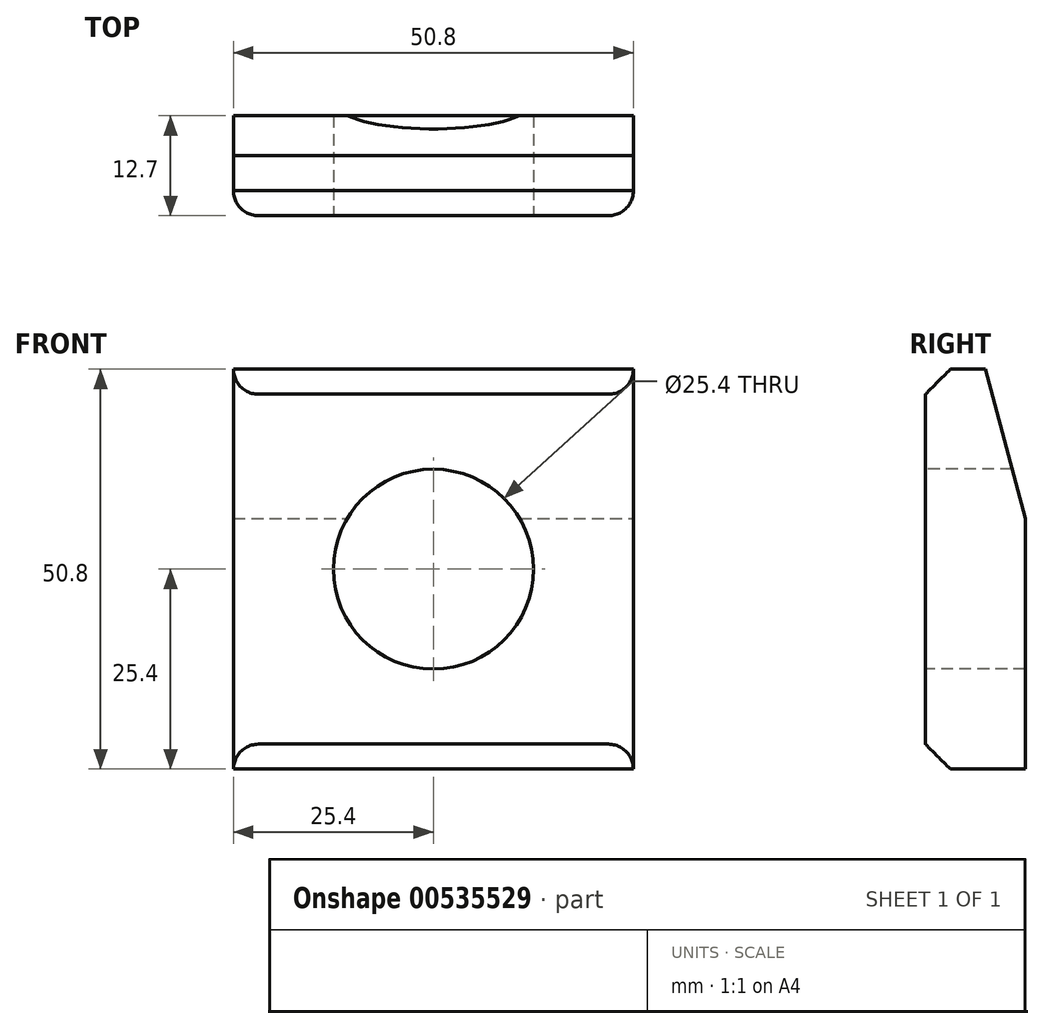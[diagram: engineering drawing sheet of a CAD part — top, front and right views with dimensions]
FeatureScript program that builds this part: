
annotation { "Feature Type Name" : "Feature", "Feature Type Description" : "" }
export const myFeature = defineFeature(function(context is Context, id is Id, definition is map)
    precondition{}
    {
        {
            var Q0;
            Q0=qCreatedBy(makeId("Front.planeOp"),FACE);
            var sketch = newSketch(context, id + "F0", { "sketchPlane" : qUnion([Q0])});
            skLineSegment(sketch, "E0.bottom", {"start": v(0, 0) * mm, "end": v(50.8, 0) * mm});
            skLineSegment(sketch, "E0.top", {"start": v(0, -50.8) * mm, "end": v(50.8, -50.8) * mm});
            skLineSegment(sketch, "E0.left", {"start": v(0, 0) * mm, "end": v(0, -50.8) * mm});
            skLineSegment(sketch, "E0.right", {"start": v(50.8, 0) * mm, "end": v(50.8, -50.8) * mm});
            skSolve(sketch);
        }
        {
            var Q0;
            Q0 = qSketchRegion(id + "F0", true);
            extrude(context, id + "F1", {"entities" : qUnion([Q0]), "depth" : 12.7 * mm, "offsetDistance" : 25.4 * mm});
        }
        {
            var Q0;
            Q0=makeQuery(id+"F1.opExtrude","CAP_FACE",FACE,{"disambiguationData":[OSD([sQuery(id+"F0.wireOp",EDGE,"E0.bottom"),sQuery(id+"F0.wireOp",EDGE,"E0.top"),sQuery(id+"F0.wireOp",EDGE,"E0.left"),sQuery(id+"F0.wireOp",EDGE,"E0.right")])],"isStart":false});
            var sketch = newSketch(context, id + "F2", { "sketchPlane" : qUnion([Q0])});
            skCircle(sketch, "E1", {"center": v(25.4, -25.4) * mm, "radius": 12.7 * mm});
            skSolve(sketch);
        }
        {
            var Q0;
            Q0 = qSketchRegion(id + "F2", true);
            extrude(context, id + "F3", {"entities" : qUnion([Q0]), "operationType" : NewBodyOperationType.REMOVE, "oppositeDirection" : true, "depth" : 25.4 * mm, "offsetDistance" : 25.4 * mm});
        }
        {
            var Q0;
            Q0=makeQuery(id+"F1.opExtrude","CAP_EDGE",EDGE,{"disambiguationData":[OSD([sQuery(id+"F0.wireOp",EDGE,"E0.left")])],"isStart":false});
            var Q1;
            Q1=makeQuery(id+"F1.opExtrude","CAP_EDGE",EDGE,{"disambiguationData":[OSD([sQuery(id+"F0.wireOp",EDGE,"E0.right")])],"isStart":false});
            fillet(context, id + "F4", {"entities" : qUnion([Q0, Q1]), "radius" : 3.17 * mm, "tangentPropagation" : true, "allowEdgeOverflow" : false});
        }
        {
            var Q0;
            Q0=makeQuery(id+"F3.boolean.opBoolean","COPY",EDGE,{"derivedFrom":makeQuery(id+"F3.opExtrude","CAP_EDGE",EDGE,{"disambiguationData":[OSD([sQuery(id+"F2.wireOp",EDGE,"E1")])],"isStart":true})});
            var Q1;
            Q1=makeQuery(id+"F1.opExtrude","CAP_EDGE",EDGE,{"disambiguationData":[OSD([sQuery(id+"F0.wireOp",EDGE,"E0.bottom")])],"isStart":false});
            var Q2;
            Q2=makeQuery(id+"F1.opExtrude","CAP_EDGE",EDGE,{"disambiguationData":[OSD([sQuery(id+"F0.wireOp",EDGE,"E0.top")])],"isStart":false});
            chamfer(context, id + "F5", {"entities" : qUnion([Q0, Q1, Q2]), "width" : 3.17 * mm});
        }
        {
            var Q0;
            Q0=makeQuery(id+"F1.opExtrude","CAP_EDGE",EDGE,{"disambiguationData":[OSD([sQuery(id+"F0.wireOp",EDGE,"E0.bottom")])],"isStart":true});
            chamfer(context, id + "F6", {"entities" : qUnion([Q0]), "chamferType" : ChamferType.OFFSET_ANGLE, "width" : 5.08 * mm, "oppositeDirection" : true, "angle" : 75 * degree, "tangentPropagation" : true});
        }
    });
